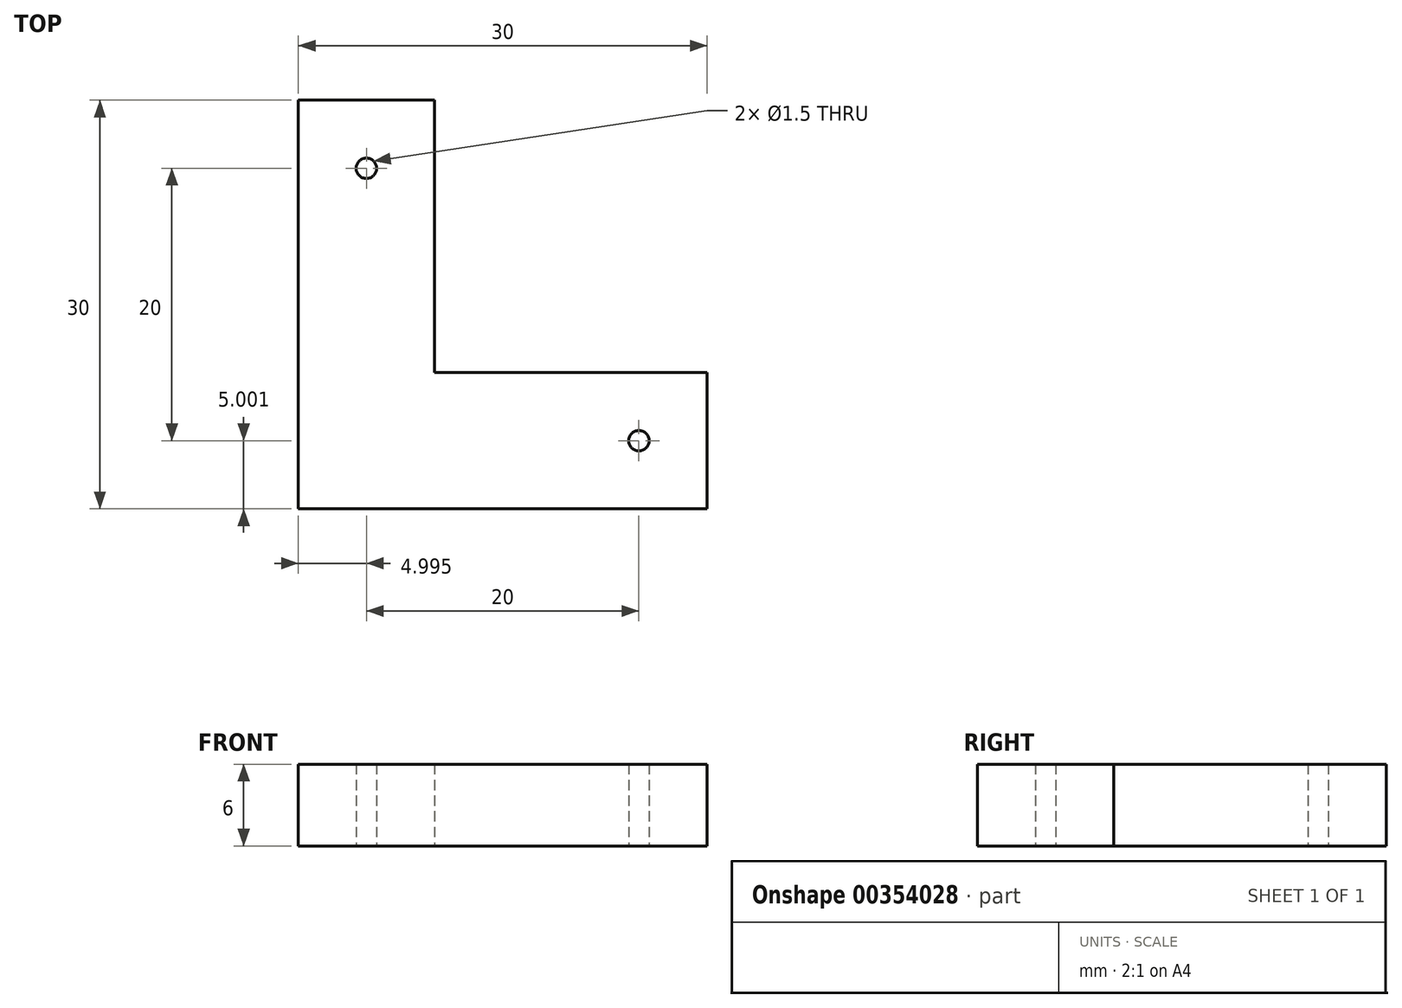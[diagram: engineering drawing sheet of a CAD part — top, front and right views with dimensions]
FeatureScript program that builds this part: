
annotation { "Feature Type Name" : "Feature", "Feature Type Description" : "" }
export const myFeature = defineFeature(function(context is Context, id is Id, definition is map)
    precondition{}
    {
        {
            var Q0;
            Q0=qCreatedBy(makeId("Top.planeOp"),FACE);
            var sketch = newSketch(context, id + "F0", { "sketchPlane" : qUnion([Q0])});
            skLineSegment(sketch, "E0.bottom", {"start": v(-2.11, 15.63) * mm, "end": v(7.89, 15.63) * mm});
            skLineSegment(sketch, "E0.top", {"start": v(-2.11, -14.37) * mm, "end": v(7.89, -14.37) * mm});
            skLineSegment(sketch, "E0.left", {"start": v(-2.11, 15.63) * mm, "end": v(-2.11, -14.37) * mm});
            skLineSegment(sketch, "E0.right", {"start": v(7.89, 15.63) * mm, "end": v(7.89, -4.37) * mm});
            skLineSegment(sketch, "E1.bottom", {"start": v(7.89, -14.37) * mm, "end": v(27.89, -14.37) * mm});
            skLineSegment(sketch, "E1.top", {"start": v(7.89, -4.37) * mm, "end": v(27.89, -4.37) * mm});
            skLineSegment(sketch, "E1.right", {"start": v(27.89, -14.37) * mm, "end": v(27.89, -4.37) * mm});
            skCircle(sketch, "E2", {"center": v(2.89, 10.63) * mm, "radius": 0.75 * mm});
            skCircle(sketch, "E3", {"center": v(22.89, -9.37) * mm, "radius": 0.75 * mm});
            skSolve(sketch);
        }
        {
            var Q0;
            Q0 = qSketchRegion(id + "F0", true);
            extrude(context, id + "F1", {"entities" : qUnion([Q0]), "depth" : 6 * mm});
        }
    });
